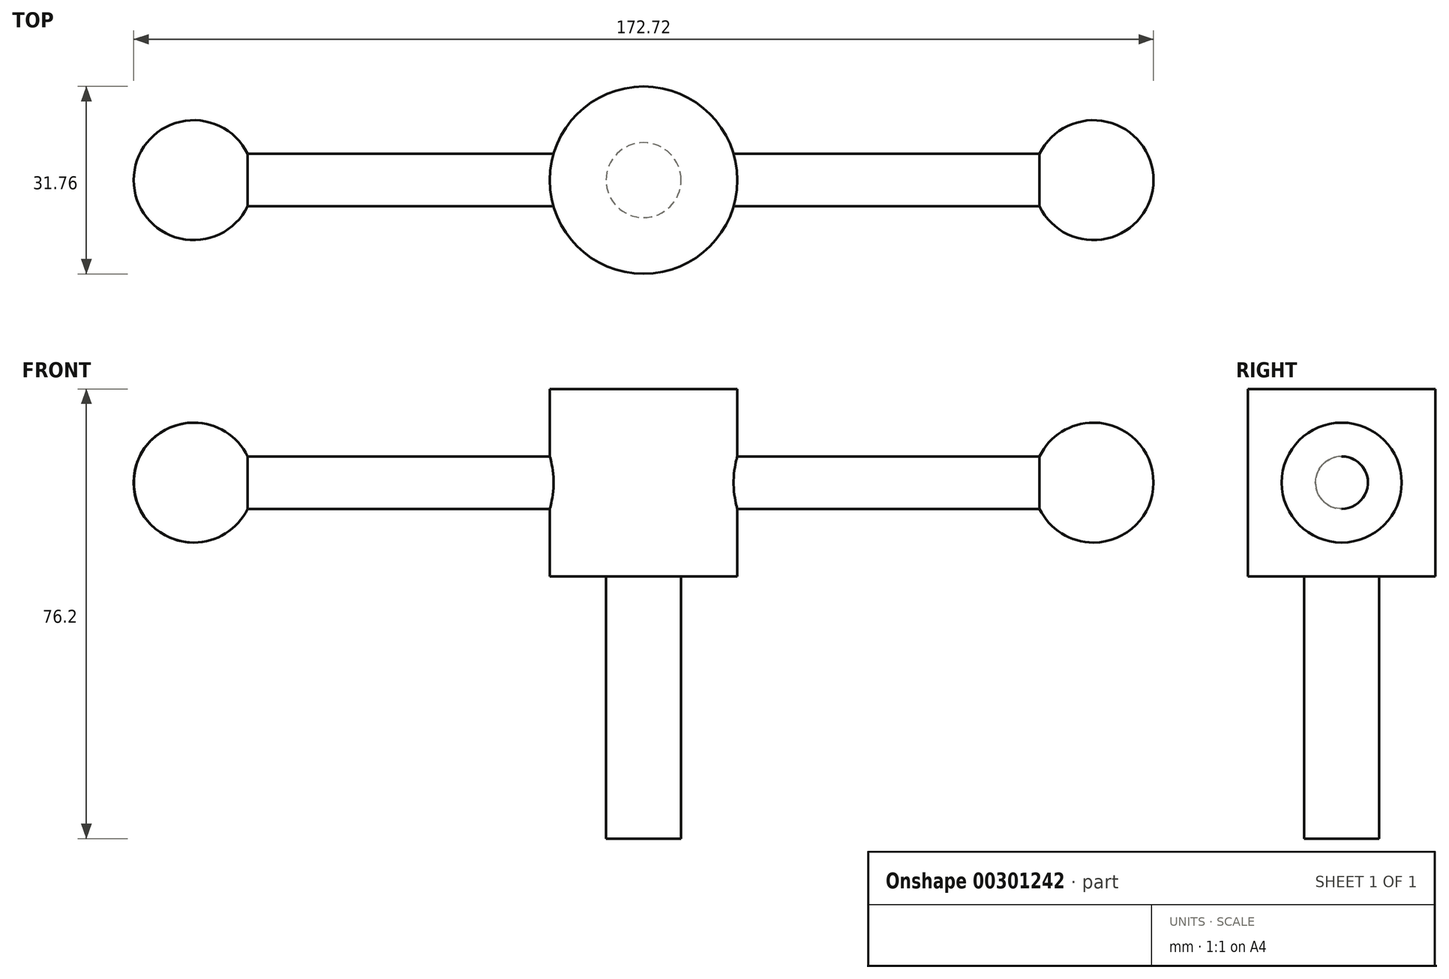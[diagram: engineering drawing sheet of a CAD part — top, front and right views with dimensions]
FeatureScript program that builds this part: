
annotation { "Feature Type Name" : "Feature", "Feature Type Description" : "" }
export const myFeature = defineFeature(function(context is Context, id is Id, definition is map)
    precondition{}
    {
        {
            var Q0;
            Q0=qCreatedBy(makeId("Top.planeOp"),FACE);
            var sketch = newSketch(context, id + "F0", { "sketchPlane" : qUnion([Q0])});
            skCircle(sketch, "E0", {"center": v(0, 0) * mm, "radius": 15.88 * mm});
            skCircle(sketch, "E1", {"center": v(0, 0) * mm, "radius": 6.35 * mm});
            skSolve(sketch);
        }
        {
            var Q0;
            Q0 = qSketchRegion(id + "F0", true);
            var Q1;
            Q1=makeQuery(id+"F0.imprint","IMPRINT",FACE,{"disambiguationData":[TD([[makeQuery(id+"F0.imprint","IMPRINT",EDGE,{"derivedFrom":sQuery(id+"F0.wireOp",EDGE,"E1")}),1.0]])]});
            extrude(context, id + "F1", {"entities" : qUnion([Q0, Q1]), "depth" : 31.75 * mm});
        }
        {
            var Q0;
            Q0=makeQuery(id+"F0.imprint","IMPRINT",FACE,{"disambiguationData":[TD([[makeQuery(id+"F0.imprint","IMPRINT",EDGE,{"derivedFrom":sQuery(id+"F0.wireOp",EDGE,"E1")}),1.0]])]});
            extrude(context, id + "F2", {"entities" : qUnion([Q0]), "operationType" : NewBodyOperationType.ADD, "oppositeDirection" : true, "depth" : 44.45 * mm});
        }
        {
            var Q0;
            Q0=qCreatedBy(makeId("Right.planeOp"),FACE);
            var sketch = newSketch(context, id + "F3", { "sketchPlane" : qUnion([Q0])});
            skCircle(sketch, "E2", {"center": v(0, 15.88) * mm, "radius": 4.45 * mm});
            skSolve(sketch);
        }
        {
            var Q0;
            Q0 = qSketchRegion(id + "F3", true);
            extrude(context, id + "F4", {"entities" : qUnion([Q0]), "operationType" : NewBodyOperationType.ADD, "endBound" : BoundingType.SYMMETRIC, "depth" : 152.4 * mm});
        }
        {
            var Q0;
            Q0=qCreatedBy(makeId("Front.planeOp"),FACE);
            var sketch = newSketch(context, id + "F5", { "sketchPlane" : qUnion([Q0])});
            skLineSegment(sketch, "E3", {"start": v(76.2, 26.04) * mm, "end": v(76.2, 5.71) * mm});
            skArc(sketch, "E4", {"start": v(76.2, 26.04) * mm, "mid": v(86.36, 15.88) * mm, "end": v(76.2, 5.71) * mm});
            skLineSegment(sketch, "E5", {"start": v(-76.2, 26.04) * mm, "end": v(-76.2, 5.71) * mm});
            skArc(sketch, "E6", {"start": v(-76.2, 26.04) * mm, "mid": v(-86.36, 15.88) * mm, "end": v(-76.2, 5.71) * mm});
            skSolve(sketch);
        }
        {
            var Q0;
            Q0=makeQuery(id+"F5.imprint","IMPRINT",FACE,{"disambiguationData":[TD([[makeQuery(id+"F5.imprint","IMPRINT",EDGE,{"derivedFrom":sQuery(id+"F5.wireOp",EDGE,"E3")}),1.0]])]});
            var Q1;
            Q1=sQuery(id+"F5.wireOp",EDGE,"E3");
            revolve(context, id + "F6", {"operationType" : NewBodyOperationType.ADD, "entities" : qUnion([Q0]), "axis" : qUnion([Q1]), "revolveType" : RevolveType.FULL});
        }
        {
            var Q0;
            Q0=makeQuery(id+"F5.imprint","IMPRINT",FACE,{"disambiguationData":[TD([[makeQuery(id+"F5.imprint","IMPRINT",EDGE,{"derivedFrom":sQuery(id+"F5.wireOp",EDGE,"E5")}),-1.0]])]});
            var Q1;
            Q1=sQuery(id+"F5.wireOp",EDGE,"E5");
            revolve(context, id + "F7", {"operationType" : NewBodyOperationType.ADD, "entities" : qUnion([Q0]), "axis" : qUnion([Q1]), "revolveType" : RevolveType.FULL});
        }
    });
